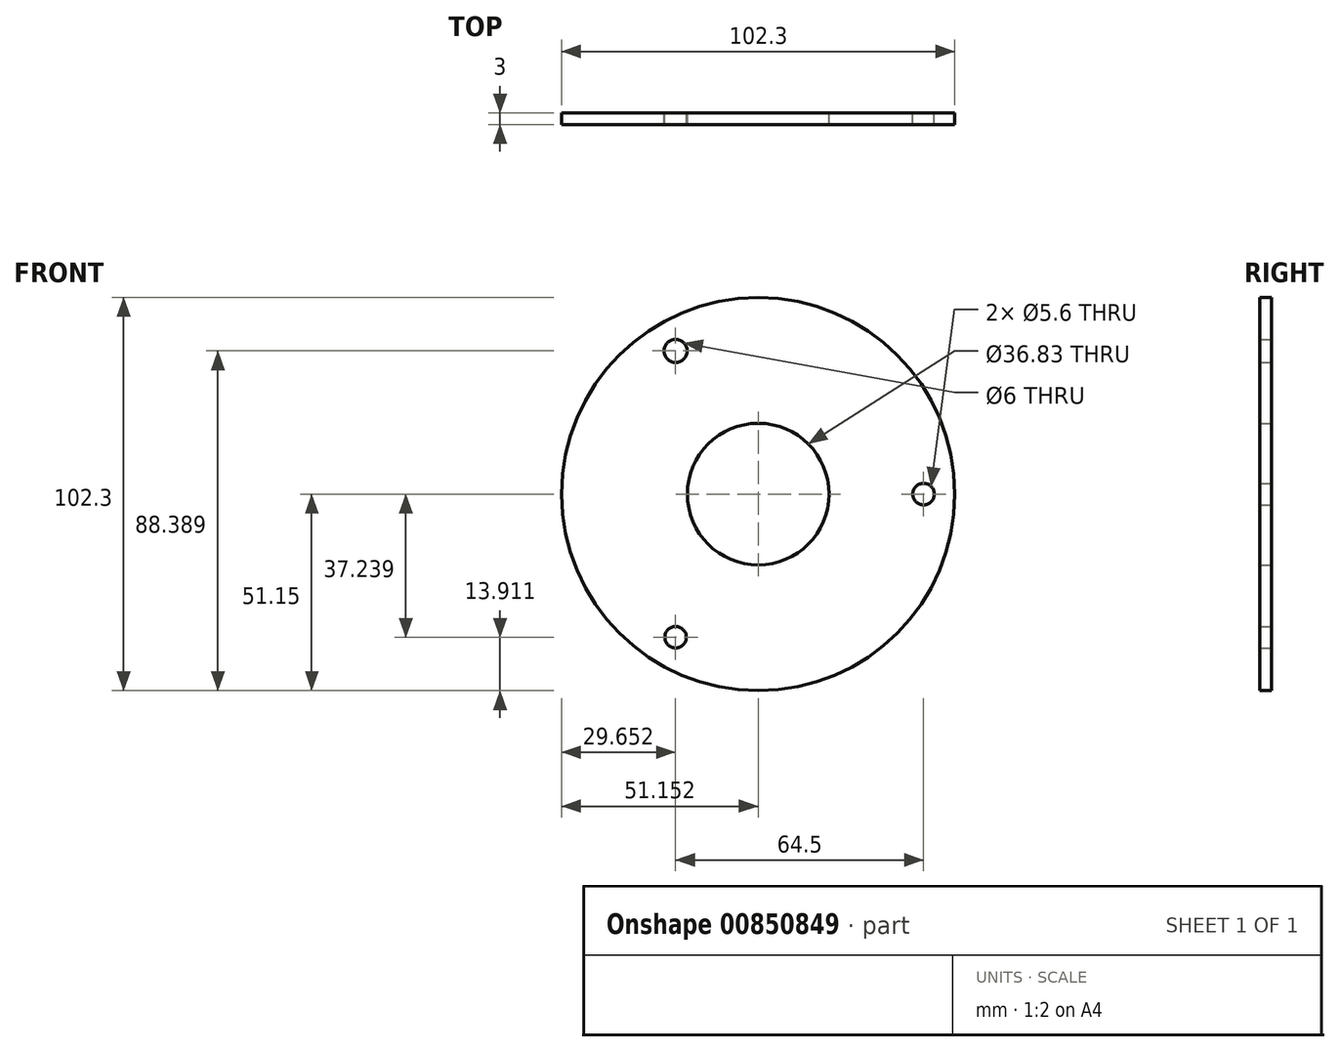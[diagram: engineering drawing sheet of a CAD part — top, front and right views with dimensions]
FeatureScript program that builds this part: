
annotation { "Feature Type Name" : "Feature", "Feature Type Description" : "" }
export const myFeature = defineFeature(function(context is Context, id is Id, definition is map)
    precondition{}
    {
        {
            var Q0;
            Q0=qCreatedBy(makeId("Front.planeOp"),FACE);
            var sketch = newSketch(context, id + "F0", { "sketchPlane" : qUnion([Q0])});
            skCircle(sketch, "E0", {"center": v(3.91, 7.34) * mm, "radius": 2.8 * mm});
            skCircle(sketch, "E1", {"center": v(-60.59, -29.9) * mm, "radius": 2.8 * mm});
            skCircle(sketch, "E2", {"center": v(-60.59, 44.58) * mm, "radius": 3 * mm});
            skCircle(sketch, "E3", {"center": v(-39.09, 7.34) * mm, "radius": 18.41 * mm});
            skCircle(sketch, "E4", {"center": v(-39.09, 7.34) * mm, "radius": 51.15 * mm});
            skSolve(sketch);
        }
        {
            var Q0;
            Q0=makeQuery(id+"F0.imprint","IMPRINT",FACE,{"disambiguationData":[TD([[makeQuery(id+"F0.imprint","IMPRINT",EDGE,{"derivedFrom":sQuery(id+"F0.wireOp",EDGE,"E0")}),-1.0]])]});
            extrude(context, id + "F1", {"entities" : qUnion([Q0]), "depth" : 3 * mm, "offsetDistance" : 25.4 * mm});
        }
    });
